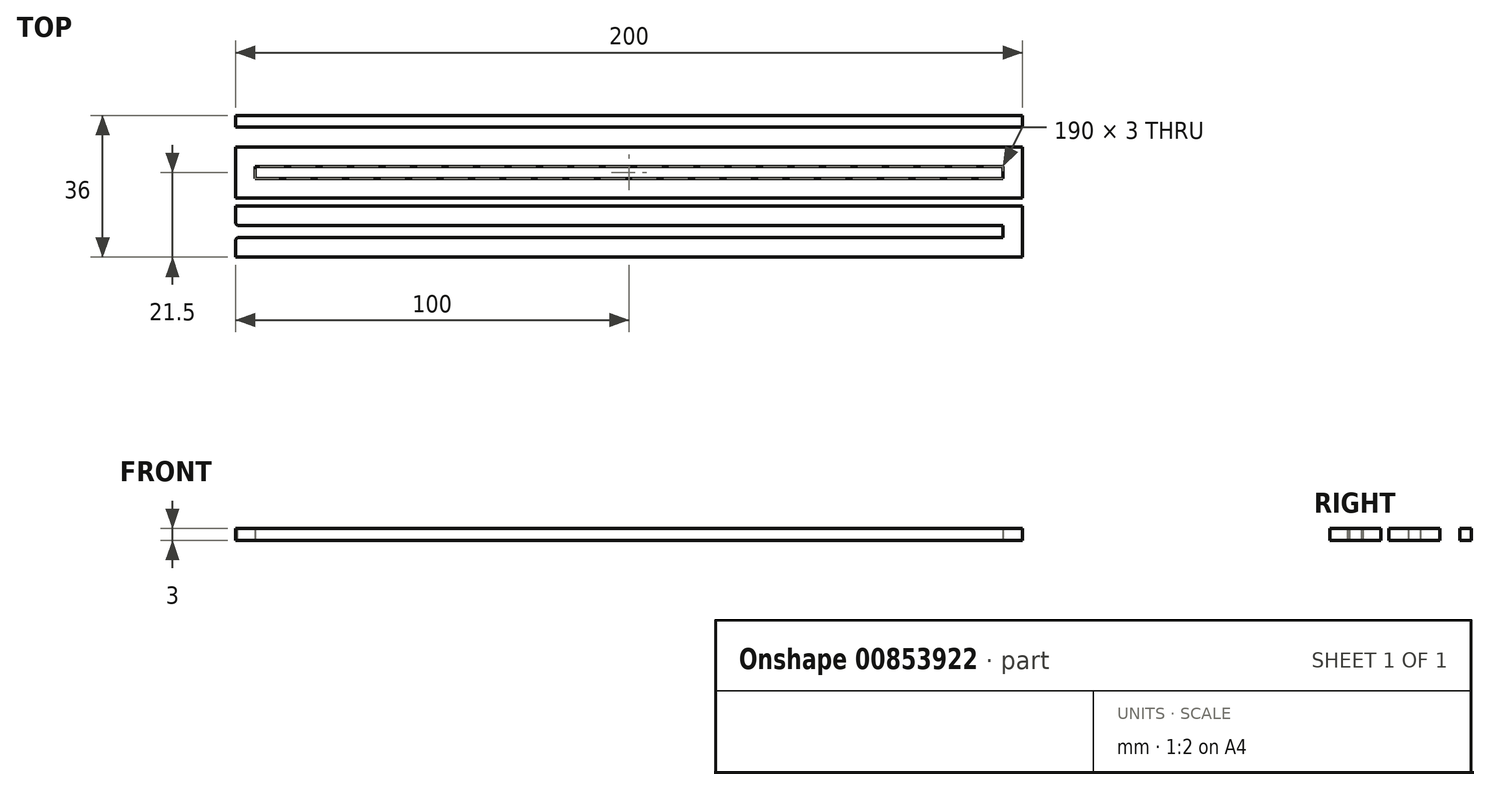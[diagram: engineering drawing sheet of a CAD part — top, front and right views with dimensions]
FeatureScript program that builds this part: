
annotation { "Feature Type Name" : "Feature", "Feature Type Description" : "" }
export const myFeature = defineFeature(function(context is Context, id is Id, definition is map)
    precondition{}
    {
        {
            var Q0;
            Q0=qCreatedBy(makeId("Top.planeOp"),FACE);
            var sketch = newSketch(context, id + "F0", { "sketchPlane" : qUnion([Q0])});
            skLineSegment(sketch, "E0.bottom", {"start": v(-100, 21.1) * mm, "end": v(100, 21.1) * mm});
            skLineSegment(sketch, "E0.top", {"start": v(-100, 24.1) * mm, "end": v(100, 24.1) * mm});
            skLineSegment(sketch, "E0.left", {"start": v(-100, 21.1) * mm, "end": v(-100, 24.1) * mm});
            skLineSegment(sketch, "E0.right", {"start": v(100, 21.1) * mm, "end": v(100, 24.1) * mm});
            skPoint(sketch, "E0.middle", {"position": v(0, 22.6) * mm});
            skLineSegment(sketch, "E1.bottom", {"start": v(95, 8.1) * mm, "end": v(-95, 8.1) * mm});
            skLineSegment(sketch, "E1.top", {"start": v(95, 11.1) * mm, "end": v(-95, 11.1) * mm});
            skLineSegment(sketch, "E1.left", {"start": v(95, 8.1) * mm, "end": v(95, 11.1) * mm});
            skLineSegment(sketch, "E1.right", {"start": v(-95, 8.1) * mm, "end": v(-95, 11.1) * mm});
            skPoint(sketch, "E1.middle", {"position": v(0, 9.6) * mm});
            skLineSegment(sketch, "E2.0", {"start": v(100, 3.1) * mm, "end": v(100, 16.1) * mm});
            skLineSegment(sketch, "E2.1", {"start": v(100, 3.1) * mm, "end": v(-100, 3.1) * mm});
            skLineSegment(sketch, "E2.2", {"start": v(-100, 3.1) * mm, "end": v(-100, 16.1) * mm});
            skLineSegment(sketch, "E2.3", {"start": v(100, 16.1) * mm, "end": v(-100, 16.1) * mm});
            skSolve(sketch);
        }
        {
            var Q0;
            Q0=makeQuery(id+"F0.imprint","IMPRINT",FACE,{"disambiguationData":[TD([[makeQuery(id+"F0.imprint","IMPRINT",EDGE,{"derivedFrom":sQuery(id+"F0.wireOp",EDGE,"E0.bottom")}),1.0]])]});
            var Q1;
            Q1=makeQuery(id+"F0.imprint","IMPRINT",FACE,{"disambiguationData":[TD([[makeQuery(id+"F0.imprint","IMPRINT",EDGE,{"derivedFrom":sQuery(id+"F0.wireOp",EDGE,"E1.bottom")}),1.0]])]});
            extrude(context, id + "F1", {"entities" : qUnion([Q0, Q1]), "depth" : 3 * mm, "offsetDistance" : 25 * mm});
        }
        {
            var Q0;
            Q0=makeQuery(id+"F1.opExtrude","SWEPT_BODY",BODY,{"disambiguationData":[OSD([sQuery(id+"F0.wireOp",EDGE,"E1.bottom"),sQuery(id+"F0.wireOp",EDGE,"E1.top"),sQuery(id+"F0.wireOp",EDGE,"E1.left"),sQuery(id+"F0.wireOp",EDGE,"E1.right"),sQuery(id+"F0.wireOp",EDGE,"E2.0"),sQuery(id+"F0.wireOp",EDGE,"E2.1"),sQuery(id+"F0.wireOp",EDGE,"E2.2"),sQuery(id+"F0.wireOp",EDGE,"E2.3")])]});
            transform(context, id + "F2", {"entities" : qUnion([Q0]), "transformType" : TransformType.TRANSLATION_3D, "dx" : 0 * mm, "dy" : -15 * mm, "dz" : 0 * mm, "makeCopy" : true});
        }
        {
            var Q0;
            Q0=makeQuery(id+"F2.opPattern","COPY",FACE,{"derivedFrom":makeQuery(id+"F1.opExtrude","SWEPT_FACE",FACE,{"disambiguationData":[OSD([sQuery(id+"F0.wireOp",EDGE,"E1.right")])]}),"instanceName":"1"});
            extrude(context, id + "F3", {"entities" : qUnion([Q0]), "operationType" : NewBodyOperationType.REMOVE, "oppositeDirection" : true, "depth" : 25 * mm, "offsetDistance" : 25 * mm});
        }
        {
            var Q0;
            Q0=makeQuery(id+"F3.boolean.opBoolean","INTERSECT",EDGE,{"derivedFrom":[makeQuery(id+"F2.opPattern","COPY",FACE,{"derivedFrom":makeQuery(id+"F1.opExtrude","SWEPT_FACE",FACE,{"disambiguationData":[OSD([sQuery(id+"F0.wireOp",EDGE,"E2.2")])]}),"instanceName":"1"}),makeQuery(id+"F3.opExtrude","SWEPT_FACE",FACE,{"disambiguationData":[OSD([sQuery(id+"F0.wireOp",EDGE,"E1.top"),sQuery(id+"F0.wireOp",EDGE,"E1.right")])]})]});
            var Q1;
            Q1=makeQuery(id+"F3.boolean.opBoolean","INTERSECT",EDGE,{"derivedFrom":[makeQuery(id+"F2.opPattern","COPY",FACE,{"derivedFrom":makeQuery(id+"F1.opExtrude","SWEPT_FACE",FACE,{"disambiguationData":[OSD([sQuery(id+"F0.wireOp",EDGE,"E2.2")])]}),"instanceName":"1"}),makeQuery(id+"F3.opExtrude","SWEPT_FACE",FACE,{"disambiguationData":[OSD([sQuery(id+"F0.wireOp",EDGE,"E1.bottom"),sQuery(id+"F0.wireOp",EDGE,"E1.right")])]})]});
            chamfer(context, id + "F4", {"entities" : qUnion([Q0, Q1]), "width" : 0.5 * mm, "tangentPropagation" : true});
        }
    });
